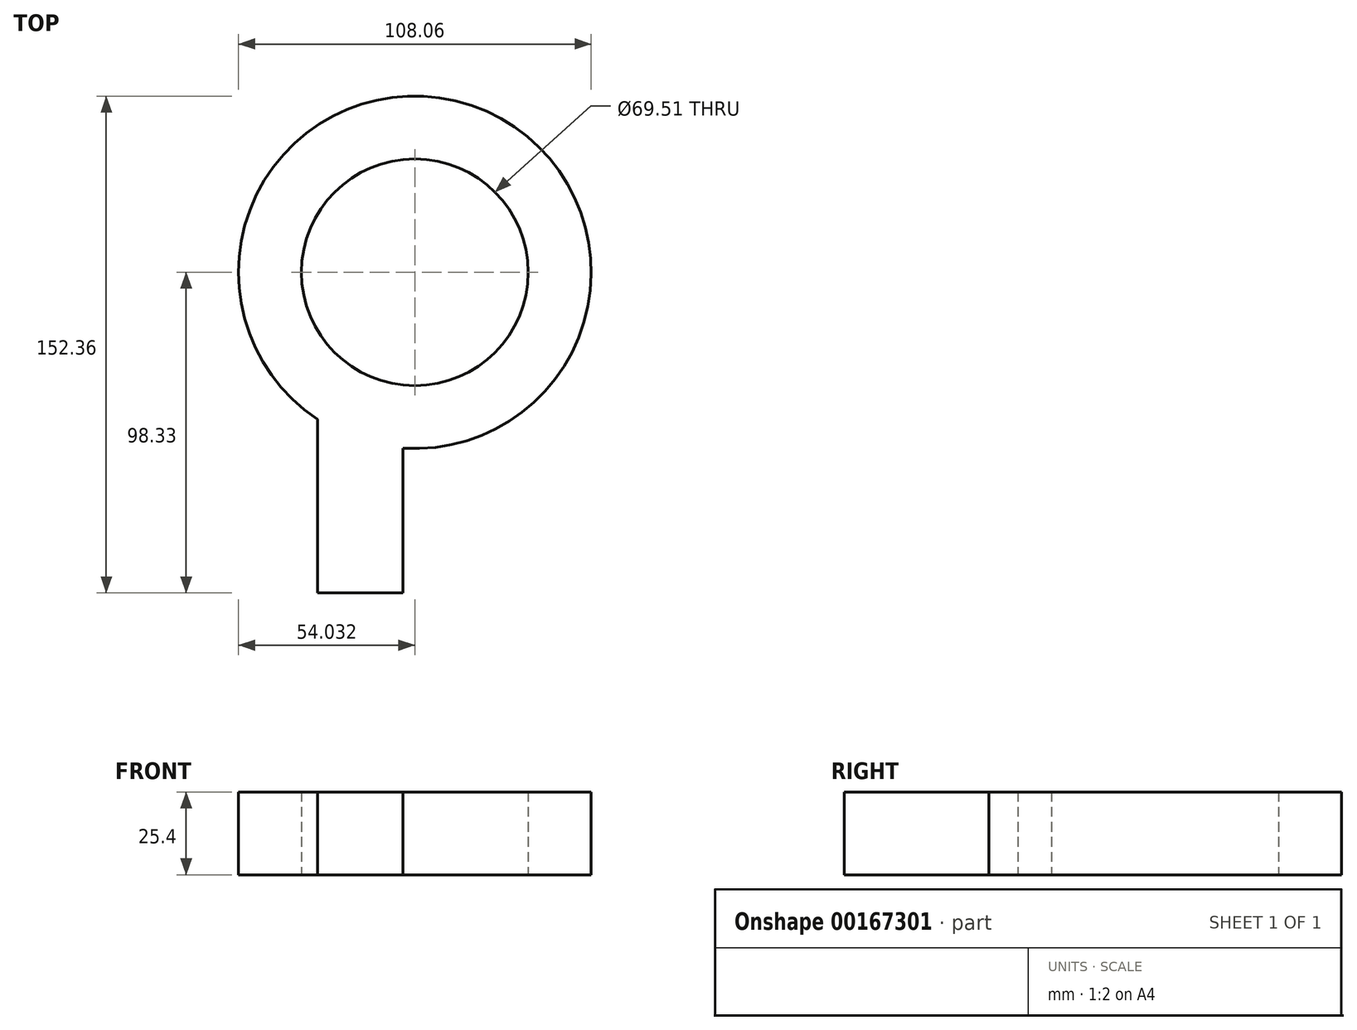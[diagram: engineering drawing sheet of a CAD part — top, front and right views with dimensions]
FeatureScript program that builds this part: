
annotation { "Feature Type Name" : "Feature", "Feature Type Description" : "" }
export const myFeature = defineFeature(function(context is Context, id is Id, definition is map)
    precondition{}
    {
        {
            var Q0;
            Q0=qCreatedBy(makeId("Top.planeOp"),FACE);
            var sketch = newSketch(context, id + "F0", { "sketchPlane" : qUnion([Q0])});
            skCircle(sketch, "E0", {"center": v(-141.46, 0) * mm, "radius": 54.03 * mm});
            skCircle(sketch, "E1", {"center": v(-141.46, 0) * mm, "radius": 34.75 * mm});
            skSolve(sketch);
        }
        {
            var Q0;
            Q0=makeQuery(id+"F0.imprint","IMPRINT",FACE,{"disambiguationData":[TD([[makeQuery(id+"F0.imprint","IMPRINT",EDGE,{"derivedFrom":sQuery(id+"F0.wireOp",EDGE,"E0")}),1.0]])]});
            extrude(context, id + "F1", {"entities" : qUnion([Q0]), "depth" : 25.4 * mm});
        }
        {
            var Q0;
            Q0=qCreatedBy(makeId("Top.planeOp"),FACE);
            var sketch = newSketch(context, id + "F2", { "sketchPlane" : qUnion([Q0])});
            skLineSegment(sketch, "E2.bottom", {"start": v(-171.24, -44.43) * mm, "end": v(-145.08, -44.43) * mm});
            skLineSegment(sketch, "E2.top", {"start": v(-171.24, -98.33) * mm, "end": v(-145.08, -98.33) * mm});
            skLineSegment(sketch, "E2.left", {"start": v(-171.24, -44.43) * mm, "end": v(-171.24, -98.33) * mm});
            skLineSegment(sketch, "E2.right", {"start": v(-145.08, -44.43) * mm, "end": v(-145.08, -98.33) * mm});
            skSolve(sketch);
        }
        {
            var Q0;
            Q0=qSketchRegion(id+"F2",true);
            extrude(context, id + "F3", {"entities" : qUnion([Q0]), "operationType" : NewBodyOperationType.ADD, "depth" : 25.4 * mm});
        }
    });
